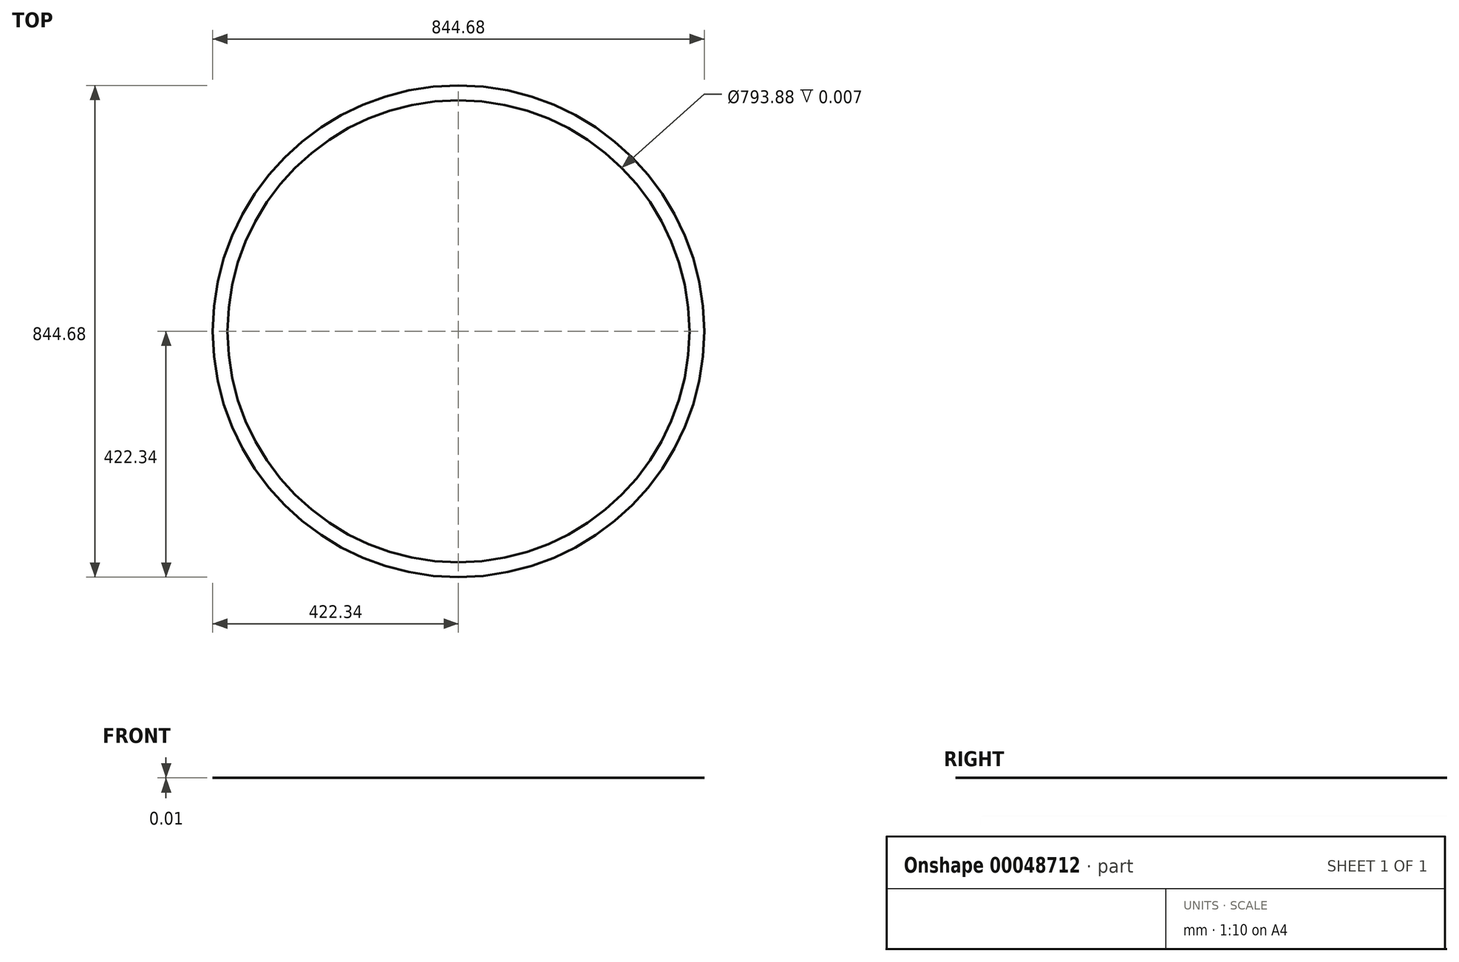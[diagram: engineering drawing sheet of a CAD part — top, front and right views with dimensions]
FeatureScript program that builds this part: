
annotation { "Feature Type Name" : "Feature", "Feature Type Description" : "" }
export const myFeature = defineFeature(function(context is Context, id is Id, definition is map)
    precondition{}
    {
        {
            var Q0;
            Q0=qCreatedBy(makeId("Top.planeOp"),FACE);
            var sketch = newSketch(context, id + "F0", { "sketchPlane" : qUnion([Q0])});
            skCircle(sketch, "E0", {"center": v(0, 0) * mm, "radius": 422.34 * mm});
            skCircle(sketch, "E1", {"center": v(0, 0) * mm, "radius": 396.94 * mm});
            skSolve(sketch);
        }
        {
            var Q0;
            Q0 = qSketchRegion(id + "F0", true);
            extrude(context, id + "F1", {"entities" : qUnion([Q0]), "depth" : 3 / 457.2 * mm});
        }
    });
